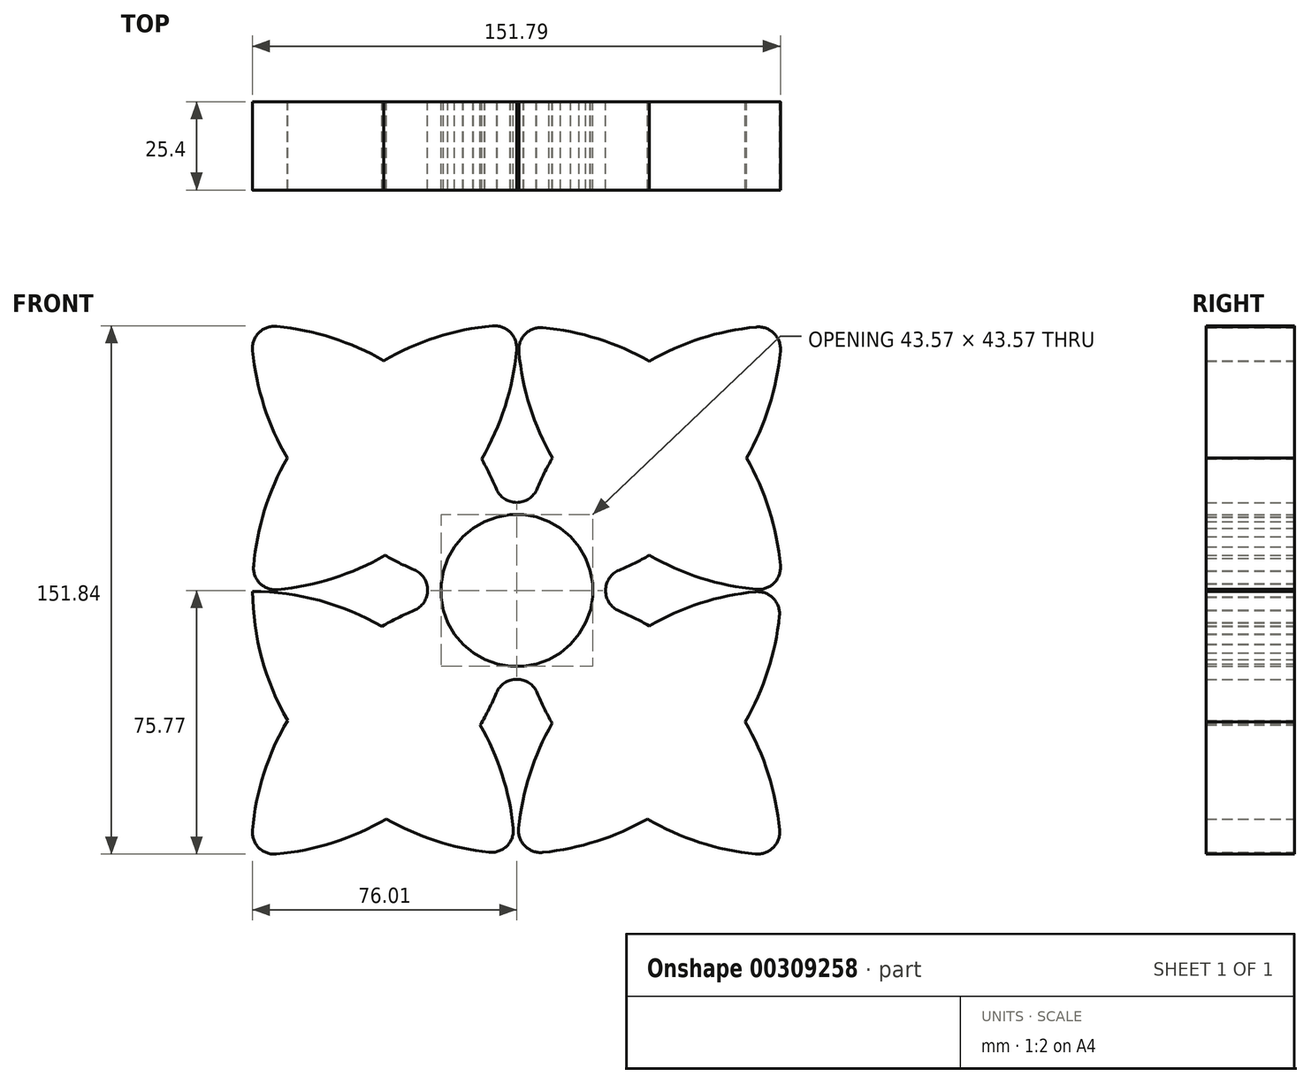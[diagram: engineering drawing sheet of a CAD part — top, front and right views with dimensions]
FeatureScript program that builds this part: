
annotation { "Feature Type Name" : "Feature", "Feature Type Description" : "" }
export const myFeature = defineFeature(function(context is Context, id is Id, definition is map)
    precondition{}
    {
        {
            var Q0;
            Q0=qCreatedBy(makeId("Front.planeOp"),FACE);
            var sketch = newSketch(context, id + "F0", { "sketchPlane" : qUnion([Q0])});
            skArc(sketch, "E0", {"start": v(5.85, -29.4) * mm, "mid": v(30.8, -61.23) * mm, "end": v(68.58, -75.7) * mm});
            skArc(sketch, "E1", {"start": v(-69.08, -75.75) * mm, "mid": v(-31.04, -61.36) * mm, "end": v(-5.87, -29.4) * mm});
            skArc(sketch, "E2", {"start": v(-5.9, 29.2) * mm, "mid": v(-31, 61.26) * mm, "end": v(-68.98, 75.92) * mm});
            skArc(sketch, "E3", {"start": v(68.8, 75.7) * mm, "mid": v(30.88, 61.18) * mm, "end": v(5.83, 29.2) * mm});
            skArc(sketch, "E4", {"start": v(-75.93, 68.98) * mm, "mid": v(-61.41, 31.08) * mm, "end": v(-29.52, 5.97) * mm});
            skArc(sketch, "E5", {"start": v(29.42, 5.84) * mm, "mid": v(61.32, 30.9) * mm, "end": v(75.73, 68.8) * mm});
            skArc(sketch, "E6", {"start": v(75.51, -68.81) * mm, "mid": v(61.2, -30.94) * mm, "end": v(29.4, -5.88) * mm});
            skArc(sketch, "E7", {"start": v(-29.55, -5.75) * mm, "mid": v(-61.56, -30.83) * mm, "end": v(-75.98, -68.85) * mm});
            skPoint(sketch, "E8.visualSharp", {"position": v(-76.29, -76.06) * mm});
            skArc(sketch, "E8.filletArc", {"start": v(-75.98, -68.85) * mm, "mid": v(-74.15, -73.91) * mm, "end": v(-69.08, -75.75) * mm});
            skPoint(sketch, "E9.visualSharp", {"position": v(-76.29, 76.29) * mm});
            skArc(sketch, "E9.filletArc", {"start": v(-68.98, 75.92) * mm, "mid": v(-74.1, 74.1) * mm, "end": v(-75.93, 68.98) * mm});
            skPoint(sketch, "E10.visualSharp", {"position": v(76.06, 76.06) * mm});
            skArc(sketch, "E10.filletArc", {"start": v(75.73, 68.8) * mm, "mid": v(73.9, 73.88) * mm, "end": v(68.8, 75.7) * mm});
            skPoint(sketch, "E11.visualSharp", {"position": v(75.82, -76.06) * mm});
            skArc(sketch, "E11.filletArc", {"start": v(68.58, -75.7) * mm, "mid": v(73.67, -73.89) * mm, "end": v(75.51, -68.81) * mm});
            skPoint(sketch, "E12.visualSharp", {"position": v(0, 0) * mm});
            skArc(sketch, "E12.filletArc", {"start": v(-5.9, 29.2) * mm, "mid": v(-0.03, 25.3) * mm, "end": v(5.83, 29.2) * mm});
            skArc(sketch, "E13.filletArc", {"start": v(5.85, -29.4) * mm, "mid": v(-0.01, -25.5) * mm, "end": v(-5.87, -29.4) * mm});
            skArc(sketch, "E14.filletArc", {"start": v(-29.55, -5.75) * mm, "mid": v(-25.63, 0.1) * mm, "end": v(-29.52, 5.97) * mm});
            skArc(sketch, "E15.filletArc", {"start": v(29.42, 5.84) * mm, "mid": v(25.51, -0.02) * mm, "end": v(29.4, -5.88) * mm});
            skCircle(sketch, "E16.cCircle", {"center": v(0, 0) * mm, "radius": 21.78 * mm, "construction": true});
            skLineSegment(sketch, "E16.0", {"start": v(12.58, -17.88) * mm, "end": v(9.28, -19.8) * mm});
            skLineSegment(sketch, "E16.1", {"start": v(9.28, -19.8) * mm, "end": v(5.7, -21.1) * mm});
            skLineSegment(sketch, "E16.2", {"start": v(5.7, -21.1) * mm, "end": v(1.95, -21.78) * mm});
            skLineSegment(sketch, "E16.3", {"start": v(1.95, -21.78) * mm, "end": v(-1.86, -21.79) * mm});
            skLineSegment(sketch, "E16.4", {"start": v(-1.86, -21.79) * mm, "end": v(-5.61, -21.13) * mm});
            skLineSegment(sketch, "E16.5", {"start": v(-5.61, -21.13) * mm, "end": v(-9.2, -19.84) * mm});
            skLineSegment(sketch, "E16.6", {"start": v(-9.2, -19.84) * mm, "end": v(-12.5, -17.94) * mm});
            skLineSegment(sketch, "E16.7", {"start": v(-12.5, -17.94) * mm, "end": v(-15.43, -15.5) * mm});
            skLineSegment(sketch, "E16.8", {"start": v(-15.43, -15.5) * mm, "end": v(-17.88, -12.58) * mm});
            skLineSegment(sketch, "E16.9", {"start": v(-17.88, -12.58) * mm, "end": v(-19.8, -9.28) * mm});
            skLineSegment(sketch, "E16.10", {"start": v(-19.8, -9.28) * mm, "end": v(-21.1, -5.7) * mm});
            skLineSegment(sketch, "E16.11", {"start": v(-21.1, -5.7) * mm, "end": v(-21.78, -1.95) * mm});
            skLineSegment(sketch, "E16.12", {"start": v(-21.78, -1.95) * mm, "end": v(-21.79, 1.86) * mm});
            skLineSegment(sketch, "E16.13", {"start": v(-21.79, 1.86) * mm, "end": v(-21.13, 5.61) * mm});
            skLineSegment(sketch, "E16.14", {"start": v(-21.13, 5.61) * mm, "end": v(-19.84, 9.2) * mm});
            skLineSegment(sketch, "E16.15", {"start": v(-19.84, 9.2) * mm, "end": v(-17.94, 12.5) * mm});
            skLineSegment(sketch, "E16.16", {"start": v(-17.94, 12.5) * mm, "end": v(-15.5, 15.43) * mm});
            skLineSegment(sketch, "E16.17", {"start": v(-15.5, 15.43) * mm, "end": v(-12.58, 17.88) * mm});
            skLineSegment(sketch, "E16.18", {"start": v(-12.58, 17.88) * mm, "end": v(-9.28, 19.8) * mm});
            skLineSegment(sketch, "E16.19", {"start": v(-9.28, 19.8) * mm, "end": v(-5.7, 21.1) * mm});
            skLineSegment(sketch, "E16.20", {"start": v(-5.7, 21.1) * mm, "end": v(-1.95, 21.78) * mm});
            skLineSegment(sketch, "E16.21", {"start": v(-1.95, 21.78) * mm, "end": v(1.86, 21.79) * mm});
            skLineSegment(sketch, "E16.22", {"start": v(1.86, 21.79) * mm, "end": v(5.61, 21.13) * mm});
            skLineSegment(sketch, "E16.23", {"start": v(5.61, 21.13) * mm, "end": v(9.2, 19.84) * mm});
            skLineSegment(sketch, "E16.24", {"start": v(9.2, 19.84) * mm, "end": v(12.5, 17.94) * mm});
            skLineSegment(sketch, "E16.25", {"start": v(12.5, 17.94) * mm, "end": v(15.43, 15.5) * mm});
            skLineSegment(sketch, "E16.26", {"start": v(15.43, 15.5) * mm, "end": v(17.88, 12.58) * mm});
            skLineSegment(sketch, "E16.27", {"start": v(17.88, 12.58) * mm, "end": v(19.8, 9.28) * mm});
            skLineSegment(sketch, "E16.28", {"start": v(19.8, 9.28) * mm, "end": v(21.1, 5.7) * mm});
            skLineSegment(sketch, "E16.29", {"start": v(21.1, 5.7) * mm, "end": v(21.78, 1.95) * mm});
            skLineSegment(sketch, "E16.30", {"start": v(21.78, 1.95) * mm, "end": v(21.79, -1.86) * mm});
            skLineSegment(sketch, "E16.31", {"start": v(21.79, -1.86) * mm, "end": v(21.13, -5.61) * mm});
            skLineSegment(sketch, "E16.32", {"start": v(21.13, -5.61) * mm, "end": v(19.84, -9.2) * mm});
            skLineSegment(sketch, "E16.33", {"start": v(19.84, -9.2) * mm, "end": v(17.94, -12.5) * mm});
            skLineSegment(sketch, "E16.34", {"start": v(17.94, -12.5) * mm, "end": v(15.5, -15.43) * mm});
            skLineSegment(sketch, "E16.35", {"start": v(15.5, -15.43) * mm, "end": v(12.58, -17.88) * mm});
            skPoint(sketch, "E16.0.midPoint", {"position": v(10.93, -18.84) * mm});
            skArc(sketch, "E17", {"start": v(-68.72, 0.23) * mm, "mid": v(-21.99, 22.33) * mm, "end": v(-0.08, 69.14) * mm});
            skArc(sketch, "E18", {"start": v(-6.98, 76.05) * mm, "mid": v(-53.82, 54.03) * mm, "end": v(-75.65, 7.11) * mm});
            skArc(sketch, "E19", {"start": v(75.75, 7.22) * mm, "mid": v(53.97, 53.72) * mm, "end": v(7.47, 75.5) * mm});
            skArc(sketch, "E20", {"start": v(0.58, 68.58) * mm, "mid": v(22.4, 22.16) * mm, "end": v(68.84, 0.33) * mm});
            skArc(sketch, "E21", {"start": v(-75.94, -0.12) * mm, "mid": v(-56.26, -50.58) * mm, "end": v(-8.02, -75.21) * mm});
            skArc(sketch, "E22", {"start": v(-1.01, -68.24) * mm, "mid": v(-25.72, -19.74) * mm, "end": v(-76.54, -0.25) * mm});
            skArc(sketch, "E23", {"start": v(68.53, -0.37) * mm, "mid": v(22.37, -22.17) * mm, "end": v(0.53, -68.33) * mm});
            skArc(sketch, "E24", {"start": v(7.5, -75.27) * mm, "mid": v(53.57, -53.4) * mm, "end": v(75.47, -7.33) * mm});
            skArc(sketch, "E25.filletArc", {"start": v(-75.65, 7.11) * mm, "mid": v(-73.8, 2.05) * mm, "end": v(-68.72, 0.23) * mm});
            skArc(sketch, "E26.filletArc", {"start": v(-0.08, 69.14) * mm, "mid": v(-1.9, 74.21) * mm, "end": v(-6.98, 76.05) * mm});
            skArc(sketch, "E27.filletArc", {"start": v(7.47, 75.5) * mm, "mid": v(2.4, 73.66) * mm, "end": v(0.58, 68.58) * mm});
            skArc(sketch, "E28.filletArc", {"start": v(68.84, 0.33) * mm, "mid": v(73.91, 2.15) * mm, "end": v(75.75, 7.22) * mm});
            skArc(sketch, "E29.filletArc", {"start": v(75.47, -7.33) * mm, "mid": v(73.65, -2.2) * mm, "end": v(68.53, -0.37) * mm});
            skArc(sketch, "E30.filletArc", {"start": v(0.53, -68.33) * mm, "mid": v(2.37, -73.45) * mm, "end": v(7.5, -75.27) * mm});
            skArc(sketch, "E31.filletArc", {"start": v(-8.02, -75.21) * mm, "mid": v(-2.85, -73.4) * mm, "end": v(-1.01, -68.24) * mm});
            skSolve(sketch);
        }
        {
            var Q0;
            Q0 = qSketchRegion(id + "F0", true);
            extrude(context, id + "F1", {"entities" : qUnion([Q0]), "depth" : 25.4 * mm});
        }
    });
